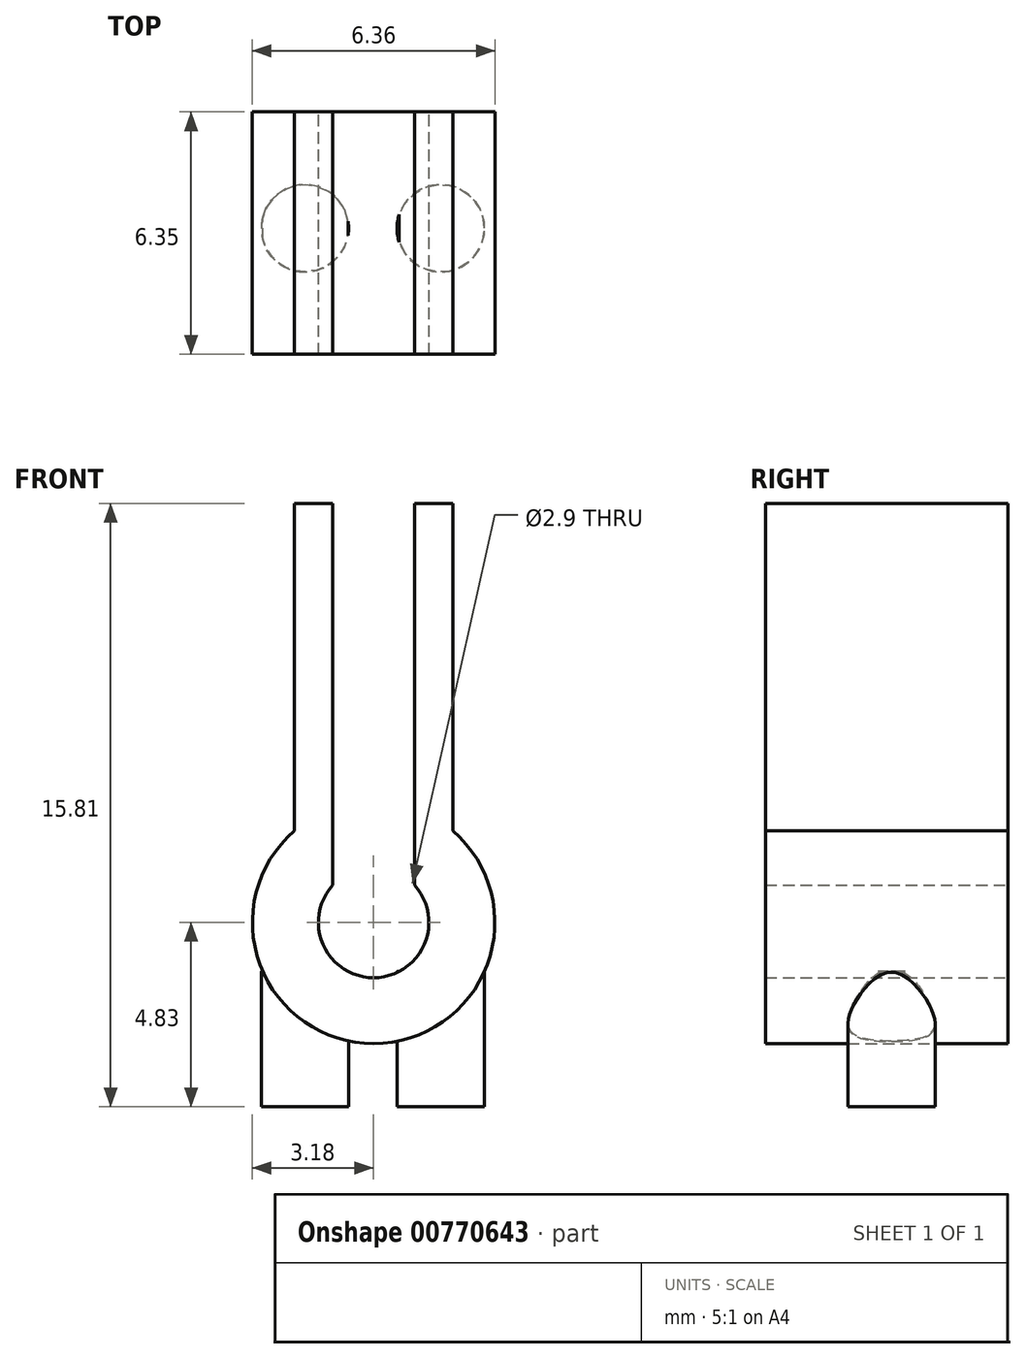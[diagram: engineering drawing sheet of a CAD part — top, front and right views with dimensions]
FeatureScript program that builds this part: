
annotation { "Feature Type Name" : "Feature", "Feature Type Description" : "" }
export const myFeature = defineFeature(function(context is Context, id is Id, definition is map)
    precondition{}
    {
        {
            var Q0;
            Q0=qCreatedBy(makeId("Front.planeOp"),FACE);
            var sketch = newSketch(context, id + "F0", { "sketchPlane" : qUnion([Q0])});
            skArc(sketch, "E0", {"start": v(-1.07, 0.98) * mm, "mid": v(0, -1.45) * mm, "end": v(1.07, 0.98) * mm});
            skLineSegment(sketch, "E1.left", {"start": v(-2.08, 4.2) * mm, "end": v(-2.08, 2.4) * mm});
            skLineSegment(sketch, "E1.right", {"start": v(-1.07, 4.2) * mm, "end": v(-1.07, 0.98) * mm});
            skLineSegment(sketch, "E2.MirrorCS", {"start": v(1.07, 4.2) * mm, "end": v(1.07, 0.98) * mm});
            skLineSegment(sketch, "E3.MirrorCS", {"start": v(2.08, 4.2) * mm, "end": v(2.08, 2.4) * mm});
            skPoint(sketch, "E4.orphan", {"position": v(-2.08, 0.57) * mm});
            skPoint(sketch, "E5.orphan", {"position": v(2.08, 0.57) * mm});
            skPoint(sketch, "E6.orphan", {"position": v(1.07, 0.57) * mm});
            skPoint(sketch, "E1.top.end.orphan", {"position": v(-1.07, 0.57) * mm});
            skLineSegment(sketch, "E7.left", {"start": v(-2.79, -1.52) * mm, "end": v(-2.79, -15.5) * mm, "construction": true});
            skLineSegment(sketch, "E7.right", {"start": v(-1.4, -2.85) * mm, "end": v(-1.4, -15.5) * mm, "construction": true});
            skLineSegment(sketch, "E8.MirrorCS", {"start": v(1.4, -2.85) * mm, "end": v(1.4, -15.5) * mm, "construction": true});
            skLineSegment(sketch, "E9.MirrorCS", {"start": v(2.79, -1.52) * mm, "end": v(2.79, -15.5) * mm, "construction": true});
            skPoint(sketch, "E10.orphan", {"position": v(-1.4, -1.52) * mm});
            skPoint(sketch, "E11.MirrorCS.end.orphan", {"position": v(1.4, -1.52) * mm});
            skPoint(sketch, "E11.MirrorCS.start.orphan", {"position": v(2.79, -1.52) * mm});
            skLineSegment(sketch, "E12", {"start": v(-2.08, 4.2) * mm, "end": v(-2.08, 10.98) * mm});
            skLineSegment(sketch, "E13", {"start": v(-2.08, 10.98) * mm, "end": v(-1.07, 10.98) * mm});
            skLineSegment(sketch, "E14", {"start": v(-1.07, 10.98) * mm, "end": v(-1.07, 4.2) * mm});
            skLineSegment(sketch, "E15.MirrorCS", {"start": v(1.07, 10.98) * mm, "end": v(1.07, 4.2) * mm});
            skLineSegment(sketch, "E16.MirrorCS", {"start": v(2.08, 4.2) * mm, "end": v(2.08, 10.98) * mm});
            skLineSegment(sketch, "E17.MirrorCS", {"start": v(2.08, 10.98) * mm, "end": v(1.07, 10.98) * mm});
            skPoint(sketch, "E18.MirrorCS.end.orphan", {"position": v(1.07, 4.2) * mm});
            skPoint(sketch, "E18.MirrorCS.start.orphan", {"position": v(2.08, 4.2) * mm});
            skPoint(sketch, "E19.MirrorCS.end.orphan", {"position": v(1.4, -15.5) * mm});
            skPoint(sketch, "E19.MirrorCS.start.orphan", {"position": v(2.79, -15.5) * mm});
            skCircle(sketch, "E20", {"center": v(0, 0) * mm, "radius": 3.18 * mm});
            skLineSegment(sketch, "E21", {"start": v(-1.07, 4.2) * mm, "end": v(-1.07, 3) * mm, "construction": true});
            skLineSegment(sketch, "E22", {"start": v(1.07, 4.2) * mm, "end": v(1.07, 3) * mm});
            skSolve(sketch);
        }
        {
            var Q0;
            {var subQ4=sQuery(id+"F0.wireOp",EDGE,"E1.left");Q0=makeQuery(id+"F0.imprint","IMPRINT",FACE,{"disambiguationData":[TD([[makeQuery(id+"F0.imprint","IMPRINT",EDGE,{"derivedFrom":subQ4}),1.0]])]});}
            var Q1;
            {var subQ5=sQuery(id+"F0.wireOp",EDGE,"E0");Q1=makeQuery(id+"F0.imprint","IMPRINT",FACE,{"disambiguationData":[TD([[makeQuery(id+"F0.imprint","IMPRINT",EDGE,{"derivedFrom":subQ5}),-1.0]])]});}
            var Q2;
            {var subQ0=sQuery(id+"F0.wireOp",EDGE,"E3.MirrorCS");Q2=makeQuery(id+"F0.imprint","IMPRINT",FACE,{"disambiguationData":[TD([[makeQuery(id+"F0.imprint","IMPRINT",EDGE,{"derivedFrom":subQ0}),-1.0]])]});}
            extrude(context, id + "F1", {"entities" : qUnion([Q0, Q1, Q2]), "depth" : 6.35 * mm, "offsetDistance" : 25.4 * mm});
        }
        {
            var Q0;
            Q0=qCreatedBy(makeId("Top.planeOp"),FACE);
            cPlane(context, id + "F2", {"entities" : qUnion([Q0]), "cplaneType" : CPlaneType.OFFSET, "offset" : 2.03 * mm, "oppositeDirection" : true, "width" : 152.4 * mm, "height" : 152.4 * mm});
        }
        {
            var Q0;
            Q0=qCreatedBy(id+"F2.planeOp",FACE);
            var sketch = newSketch(context, id + "F3", { "sketchPlane" : qUnion([Q0])});
            skCircle(sketch, "E23", {"center": v(-1.8, -3.05) * mm, "radius": 1.14 * mm});
            skCircle(sketch, "E24", {"center": v(1.76, -3.05) * mm, "radius": 1.14 * mm});
            skSolve(sketch);
        }
        {
            var Q0;
            Q0=qSketchRegion(id+"F3",true);
            extrude(context, id + "F4", {"entities" : qUnion([Q0]), "operationType" : NewBodyOperationType.ADD, "depth" : 0.75 * mm, "offsetDistance" : 25.4 * mm, "hasSecondDirection" : true, "secondDirectionOppositeDirection" : true, "secondDirectionDepth" : 2.8 * mm});
        }
    });
